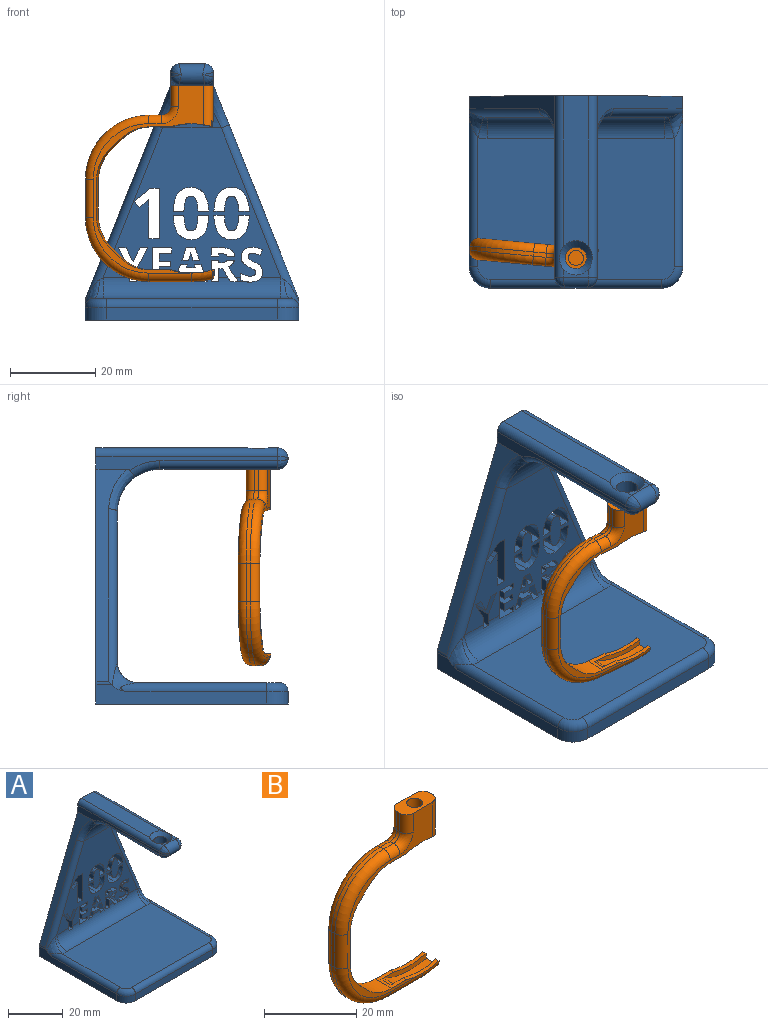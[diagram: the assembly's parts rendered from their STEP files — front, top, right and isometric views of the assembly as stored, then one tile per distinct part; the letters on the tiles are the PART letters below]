
ASSEMBLY  parts=2 mates=1
PART A: 194 faces, bbox 53.3x46.3x60.9 mm
  f0: plane 41.69x35.07mm, normal (0,-1,0), area 708mm2, adj f10,f11,f12,f15,f16,f17,f18,f19
  f1: plane 3.43x0.89mm, normal (0,-1,0), area 2.8mm2, adj f89,f90,f91,f191
  f2: plane 35.35x6mm, normal (0,0,1), area 206.5mm2, adj f9,f179,f180,f188
  f3: plane 2.17x2.04mm, normal (0,-1,0), area 3.1mm2, adj f97,f98,f99,f191
  f4: plane 40.93x5.54mm, normal (-1,0,0), area 127.7mm2, adj f5,f9,f162,f164,f169,f171,f193
  f5: plane 50x45mm, normal (0,0,-1), area 2239.3mm2, adj f4,f6,f8,f9,f161,f162
  f6: plane 40.93x5.54mm, normal (1,0,0), area 127.7mm2, adj f5,f9,f161,f167,f175,f177,f189
  f7: plane 46x33.29mm, normal (0,0,1), area 1514.6mm2, adj f164,f165,f166,f167,f168,f190,f191,f192
  f8: plane 40x3mm, normal (0,-1,0), area 120mm2, adj f5,f161,f162,f166
  f9: plane 60x50mm, normal (0,1,0), area 1525.4mm2, adj f2,f4,f5,f6,f10,f11,f12,f13
  f10: extruded ~5x1.53mm, area 9.4mm2, adj f0,f9,f11,f158
  f11: extruded ~5x1.31mm, area 7mm2, adj f0,f9,f10,f12
  f12: extruded ~5.02x1.69mm, area 9.7mm2, adj f0,f9,f11,f13,f191
  f13: extruded ~5.12x2.15mm, area 11.6mm2, adj f9,f12,f14,f191
  f14: extruded ~5.12x2.25mm, area 11.8mm2, adj f9,f13,f15,f191
  f15: plane 5.04x1.56mm, normal (1,0,0), area 7.8mm2, adj f0,f9,f14,f16,f191
  f16: extruded ~5x1.36mm, area 7.3mm2, adj f0,f9,f15,f17
  f17: extruded ~5x1.02mm, area 5.2mm2, adj f0,f9,f16,f18
  f18: extruded ~5x0.85mm, area 4.4mm2, adj f0,f9,f17,f19
  f19: extruded ~5x0.63mm, area 3.6mm2, adj f0,f9,f18,f20
  f20: extruded ~5x0.42mm, area 2.2mm2, adj f0,f9,f19,f21
  f21: extruded ~5x0.38mm, area 2.6mm2, adj f0,f9,f20,f22
  f22: extruded ~5x1.03mm, area 5.8mm2, adj f0,f9,f21,f23
  f23: extruded ~5x1.09mm, area 6.4mm2, adj f0,f9,f22,f24
  f24: extruded ~5x0.73mm, area 4.7mm2, adj f0,f9,f23,f25
  f25: extruded ~5x0.98mm, area 5mm2, adj f0,f9,f24,f26
  f26: extruded ~5x1.66mm, area 9.3mm2, adj f0,f9,f25,f27
  f27: extruded ~5x1.97mm, area 10.5mm2, adj f0,f9,f26,f28
  f28: extruded ~5x1.18mm, area 6mm2, adj f0,f9,f27,f29
  f29: extruded ~5x1.17mm, area 6.2mm2, adj f0,f9,f28,f30
  f30: plane 5x1.31mm, normal (-0.92,0,0.38), area 7.1mm2, adj f0,f9,f29,f31
  f31: extruded ~5x1.05mm, area 5.6mm2, adj f0,f9,f30,f32
  f32: extruded ~5x0.82mm, area 4.1mm2, adj f0,f9,f31,f33
  f33: extruded ~5x0.73mm, area 3.9mm2, adj f0,f9,f32,f34
  f34: extruded ~5x0.58mm, area 3.3mm2, adj f0,f9,f33,f35
  f35: extruded ~5x0.39mm, area 2mm2, adj f0,f9,f34,f36
  f36: extruded ~5x0.33mm, area 2.3mm2, adj f0,f9,f35,f158
  f37: plane 5x2.89mm, normal (0,0,-1), area 14.4mm2, adj f0,f9,f38,f146
  f38: plane 5.1x1.39mm, normal (-1,0,0), area 7mm2, adj f0,f9,f37,f39,f191
  f39: plane 5.1x4.57mm, normal (0,0,1), area 23.3mm2, adj f9,f38,f40,f191
  f40: plane 7.93x5.1mm, normal (1,0,0), area 39.7mm2, adj f0,f9,f39,f41,f191
  f41: plane 5x4.57mm, normal (0,0,-1), area 22.8mm2, adj f0,f9,f40,f42
  f42: plane 5x1.38mm, normal (-1,0,0), area 6.9mm2, adj f0,f9,f41,f43
  f43: plane 5x2.89mm, normal (0,0,1), area 14.4mm2, adj f0,f9,f42,f44
  f44: plane 5x1.74mm, normal (-1,0,0), area 8.7mm2, adj f0,f9,f43,f45
  f45: plane 5x2.69mm, normal (0,0,-1), area 13.4mm2, adj f0,f9,f44,f46
  f46: plane 5x1.38mm, normal (-1,0,0), area 6.9mm2, adj f0,f9,f45,f47
  f47: plane 5x2.69mm, normal (0,0,1), area 13.4mm2, adj f0,f9,f46,f146
  f48: plane 5x1.82mm, normal (0,0,-1), area 9.1mm2, adj f0,f9,f49,f147
  f49: plane 5x3.27mm, normal (-0.89,0,-0.45), area 18.3mm2, adj f0,f9,f48,f50
  f50: plane 5x3.27mm, normal (0.89,0,-0.45), area 18.3mm2, adj f0,f9,f49,f51
  f51: plane 5x1.81mm, normal (0,0,-1), area 9.1mm2, adj f0,f9,f50,f52
  f52: plane 5x4.85mm, normal (-0.88,0,0.48), area 27.6mm2, adj f0,f9,f51,f53
  f53: plane 5.1x3.09mm, normal (-1,0,0), area 15.5mm2, adj f0,f9,f52,f54,f191
  f54: plane 5.1x1.67mm, normal (0,0,1), area 8.5mm2, adj f9,f53,f55,f191
  f55: plane 5.1x3.03mm, normal (1,0,0), area 15.2mm2, adj f0,f9,f54,f147,f191
  f56: plane 5x2.5mm, normal (0,0,1), area 12.5mm2, adj f0,f9,f57,f148
  f57: extruded ~5x4.09mm, area 21.3mm2, adj f0,f9,f56,f58
  f58: extruded ~5x3.13mm, area 18.1mm2, adj f0,f9,f57,f59
  f59: extruded ~5x3.11mm, area 18.2mm2, adj f0,f9,f58,f60
  f60: extruded ~5x4.02mm, area 21mm2, adj f0,f9,f59,f61
  f61: plane 5x2.5mm, normal (0,0,1), area 12.5mm2, adj f0,f9,f60,f62
  f62: extruded ~5x2.59mm, area 13.2mm2, adj f0,f9,f61,f63
  f63: extruded ~5x1.27mm, area 8.5mm2, adj f0,f9,f62,f64
  f64: extruded ~5x1.27mm, area 8.5mm2, adj f0,f9,f63,f148
  f65: plane 5x2.07mm, normal (0,0,-1), area 10.3mm2, adj f0,f9,f66,f149
  f66: plane 11.9x5mm, normal (-1,0,0), area 59.5mm2, adj f0,f9,f65,f67
  f67: plane 5x2.52mm, normal (0,0,1), area 12.6mm2, adj f0,f9,f66,f68
  f68: plane 6.89x5mm, normal (1,0,0), area 34.4mm2, adj f0,f9,f67,f69
  f69: plane 5x1.13mm, normal (1,0,-0.02), area 5.7mm2, adj f0,f9,f68,f70
  f70: plane 5x1.24mm, normal (1,0,-0.03), area 6.2mm2, adj f0,f9,f69,f71
  f71: extruded ~5x0.87mm, area 6mm2, adj f0,f9,f70,f72
  f72: plane 5x1.37mm, normal (-0.63,0,0.78), area 8.8mm2, adj f0,f9,f71,f73
  f73: plane 5x1.51mm, normal (0.78,0,0.63), area 9.7mm2, adj f0,f9,f72,f149
  f74: plane 5x1.57mm, normal (0,0,1), area 7.9mm2, adj f0,f9,f75,f150
  f75: plane 5x2.97mm, normal (0.94,0,-0.33), area 15.7mm2, adj f0,f9,f74,f76
  f76: plane 5x2.06mm, normal (0,0,-1), area 10.3mm2, adj f0,f9,f75,f77
  f77: plane 5x2.97mm, normal (-0.94,0,-0.33), area 15.7mm2, adj f0,f9,f76,f78
  f78: plane 5x1.55mm, normal (0,0,1), area 7.8mm2, adj f0,f9,f77,f79
  f79: extruded ~5x1.2mm, area 6.3mm2, adj f0,f9,f78,f80
  f80: extruded ~5x0.53mm, area 2.8mm2, adj f0,f9,f79,f150
  f81: plane 5.1x4mm, normal (0.94,0,-0.33), area 21.2mm2, adj f0,f9,f82,f151,f191
  f82: plane 5x1.62mm, normal (0,0,-1), area 8.1mm2, adj f0,f9,f81,f83
  f83: extruded ~5x0.7mm, area 3.7mm2, adj f0,f9,f82,f84
  f84: plane 5x2.07mm, normal (0,0,-1), area 10.3mm2, adj f0,f9,f83,f85
  f85: extruded ~5x0.7mm, area 3.7mm2, adj f0,f9,f84,f86
  f86: plane 5x1.6mm, normal (0,0,-1), area 8mm2, adj f0,f9,f85,f87
  f87: plane 5.1x4mm, normal (-0.94,0,-0.33), area 21.2mm2, adj f0,f9,f86,f88,f191
  f88: plane 5.1x1.81mm, normal (0,0,1), area 9.2mm2, adj f9,f87,f89,f191
  f89: plane 5.1x1.89mm, normal (0.96,0,0.29), area 9.9mm2, adj f1,f9,f88,f90,f191
  f90: plane 5x2.89mm, normal (0,0,1), area 14.5mm2, adj f1,f9,f89,f91
  f91: plane 5.1x1.89mm, normal (-0.96,0,0.29), area 9.9mm2, adj f1,f9,f90,f151,f191
  f92: plane 5x1.74mm, normal (0,0,-1), area 8.7mm2, adj f0,f9,f93,f152
  f93: extruded ~5x0.69mm, area 3.8mm2, adj f0,f9,f92,f94
  f94: extruded ~5x1.09mm, area 7mm2, adj f0,f9,f93,f95
  f95: extruded ~5.1x3.46mm, area 20.9mm2, adj f0,f9,f94,f96,f191
  f96: plane 5.1x1.87mm, normal (0,0,1), area 9.5mm2, adj f9,f95,f97,f191
  f97: plane 5.1x3.05mm, normal (0.85,0,0.53), area 18mm2, adj f3,f9,f96,f98,f191
  f98: plane 5x0.89mm, normal (0,0,1), area 4.5mm2, adj f3,f9,f97,f99
  f99: plane 5.1x3.04mm, normal (-1,0,0), area 15.3mm2, adj f3,f9,f98,f100,f191
  f100: plane 5.1x1.68mm, normal (0,0,1), area 8.6mm2, adj f9,f99,f101,f191
  f101: plane 5.1x5mm, normal (1,0,0), area 25mm2, adj f0,f9,f100,f102,f191
  f102: plane 5x1.68mm, normal (0,0,-1), area 8.4mm2, adj f0,f9,f101,f103
  f103: plane 5x0.59mm, normal (-1,0,0), area 2.9mm2, adj f0,f9,f102,f104
  f104: plane 5x0.54mm, normal (0,0,-1), area 2.7mm2, adj f0,f9,f103,f105
  f105: extruded ~5x1.18mm, area 6.1mm2, adj f0,f9,f104,f152
  f106: extruded ~5x1.34mm, area 7.9mm2, adj f0,f9,f107,f153
  f107: plane 5x1.77mm, normal (0,0,1), area 8.8mm2, adj f0,f9,f106,f108
  f108: extruded ~5x0.32mm, area 2.2mm2, adj f0,f9,f107,f109
  f109: extruded ~5x1.2mm, area 6.2mm2, adj f0,f9,f108,f110
  f110: plane 5x0.51mm, normal (0,0,1), area 2.6mm2, adj f0,f9,f109,f111
  f111: plane 5x0.55mm, normal (-1,0,0), area 2.8mm2, adj f0,f9,f110,f112
  f112: plane 5x1.68mm, normal (0,0,1), area 8.4mm2, adj f0,f9,f111,f113
  f113: plane 5x1.93mm, normal (1,0,0), area 9.7mm2, adj f0,f9,f112,f114
  f114: plane 5x2.31mm, normal (0,0,-1), area 11.6mm2, adj f0,f9,f113,f153
  f115: plane 5x2.5mm, normal (0,0,-1), area 12.5mm2, adj f0,f9,f116,f154
  f116: extruded ~5x4.17mm, area 21.7mm2, adj f0,f9,f115,f117
  f117: extruded ~5x3.15mm, area 18.2mm2, adj f0,f9,f116,f118
  f118: extruded ~5x3.11mm, area 18.1mm2, adj f0,f9,f117,f119
  f119: extruded ~5x4.12mm, area 21.5mm2, adj f0,f9,f118,f120
  f120: plane 5x2.5mm, normal (0,0,-1), area 12.5mm2, adj f0,f9,f119,f121
  f121: extruded ~5x2.69mm, area 13.6mm2, adj f0,f9,f120,f122
  f122: extruded ~5x1.27mm, area 8.5mm2, adj f0,f9,f121,f123
  f123: extruded ~5x1.27mm, area 8.5mm2, adj f0,f9,f122,f154
  f124: plane 5x2.5mm, normal (0,0,-1), area 12.5mm2, adj f0,f9,f125,f155
  f125: extruded ~5x4.17mm, area 21.7mm2, adj f0,f9,f124,f126
  f126: extruded ~5x3.15mm, area 18.2mm2, adj f0,f9,f125,f127
  f127: extruded ~5x3.11mm, area 18.1mm2, adj f0,f9,f126,f128
  f128: extruded ~5x4.12mm, area 21.5mm2, adj f0,f9,f127,f129
  f129: plane 5x2.5mm, normal (0,0,-1), area 12.5mm2, adj f0,f9,f128,f130
  f130: extruded ~5x2.69mm, area 13.6mm2, adj f0,f9,f129,f131
  f131: extruded ~5x1.27mm, area 8.5mm2, adj f0,f9,f130,f132
  f132: extruded ~5x1.27mm, area 8.5mm2, adj f0,f9,f131,f155
  f133: extruded ~5x4.02mm, area 21mm2, adj f0,f9,f134,f156
  f134: plane 5x2.5mm, normal (0,0,1), area 12.5mm2, adj f0,f9,f133,f135
  f135: extruded ~5x2.59mm, area 13.2mm2, adj f0,f9,f134,f136
  f136: extruded ~5x1.27mm, area 8.5mm2, adj f0,f9,f135,f137
  f137: extruded ~5x1.27mm, area 8.5mm2, adj f0,f9,f136,f138
  f138: extruded ~5x2.59mm, area 13.2mm2, adj f0,f9,f137,f139
  f139: plane 5x2.5mm, normal (0,0,1), area 12.5mm2, adj f0,f9,f138,f140
  f140: extruded ~5x4.09mm, area 21.3mm2, adj f0,f9,f139,f141
  f141: extruded ~5x3.13mm, area 18.1mm2, adj f0,f9,f140,f156
  f142: plane 42.5x3.24mm, normal (-1,0,0), area 63.6mm2, adj f9,f143,f170,f172,f173,f180,f183
  f143: plane 49.64x19.86mm, normal (-0.93,0,0.37), area 173.7mm2, adj f9,f142,f169,f171,f173
  f144: plane 49.64x19.86mm, normal (0.93,0,0.37), area 173.7mm2, adj f9,f145,f175,f177,f178
  f145: plane 42.5x3.24mm, normal (1,0,0), area 63.6mm2, adj f9,f144,f174,f176,f178,f179,f184
  f146: plane 5x2.05mm, normal (-1,0,0), area 10.2mm2, adj f0,f9,f37,f47
  f147: plane 5x4.9mm, normal (0.88,0,0.47), area 27.8mm2, adj f0,f9,f48,f55
  f148: extruded ~5x2.59mm, area 13.2mm2, adj f0,f9,f56,f64
  f149: plane 5x3.83mm, normal (0.62,0,-0.78), area 24.5mm2, adj f0,f9,f65,f73
  f150: extruded ~5x1.73mm, area 9mm2, adj f0,f9,f74,f80
  f151: plane 5.1x1.81mm, normal (0,0,1), area 9.2mm2, adj f9,f81,f91,f191
  f152: extruded ~5x0.32mm, area 2.1mm2, adj f0,f9,f92,f105
  f153: extruded ~5x2.39mm, area 12.5mm2, adj f0,f9,f106,f114
  f154: extruded ~5x2.68mm, area 13.6mm2, adj f0,f9,f115,f123
  f155: extruded ~5x2.68mm, area 13.6mm2, adj f0,f9,f124,f132
  f156: extruded ~5x3.11mm, area 18.2mm2, adj f0,f9,f133,f141
  f157: plane 6x1.85mm, normal (0,0,1), area 5.5mm2, adj f179,f180,f185,f188
  f158: extruded ~5x1.07mm, area 6mm2, adj f0,f9,f10,f36
  f159: plane 27.5x6mm, normal (0,0,-1), area 145.4mm2, adj f160,f163,f170,f174,f185
  f160: cylinder r=2.5mm len=5mm, axis (0,0,1), area 55mm2, adj f159,f188
  f161: cylinder r=5mm len=5mm, axis (0,0,-1), area 23.6mm2, adj f5,f6,f8,f168
  f162: cylinder r=5mm len=5mm, axis (0,0,1), area 23.6mm2, adj f4,f5,f8,f165
  f163: cylinder r=10mm len=13.69mm, axis (-1,0,0), area 130mm2, adj f0,f159,f172,f173,f176,f178
  f164: cylinder r=2mm len=34.17mm, axis (0,-1,0), area 102.7mm2, adj f4,f7,f165,f193
  f165: torus R=3mm, axis (0,0,1), area 21.1mm2, adj f7,f162,f164,f166
  f166: cylinder r=2mm len=40mm, axis (1,0,0), area 125.7mm2, adj f7,f8,f165,f168
  f167: cylinder r=2mm len=34.17mm, axis (0,1,0), area 102.7mm2, adj f6,f7,f168,f189
  f168: torus R=3mm, axis (0,0,1), area 21.1mm2, adj f7,f161,f166,f167
  f169: cylinder r=2mm len=3.74mm, axis (0,1,0), area 2.6mm2, adj f4,f9,f143,f171
  f170: cylinder r=2mm len=27.5mm, axis (0,1,0), area 86.4mm2, adj f142,f159,f172,f182
  f171: cylinder r=2mm len=41.9mm, axis (0.37,0,0.93), area 128.9mm2, adj f0,f4,f143,f169,f173,f192,f193
  f172: torus R=12mm, axis (1,0,0), area 21.1mm2, adj f142,f163,f170,f173
  f173: bspline ~10.36x6.07mm, area 36mm2, adj f142,f143,f163,f171,f172
  f174: cylinder r=2mm len=27.5mm, axis (0,-1,0), area 86.4mm2, adj f145,f159,f176,f181
  f175: cylinder r=2mm len=3.74mm, axis (0,1,0), area 2.6mm2, adj f6,f9,f144,f177
  f176: torus R=12mm, axis (1,0,0), area 21.1mm2, adj f145,f163,f174,f178
  f177: cylinder r=2mm len=41.9mm, axis (0.37,0,-0.93), area 128.9mm2, adj f0,f6,f144,f175,f178,f189,f190
  f178: bspline ~10.36x6.07mm, area 36mm2, adj f144,f145,f163,f176,f177
  f179: cylinder r=2mm len=42.5mm, axis (0,1,0), area 131.3mm2, adj f2,f9,f145,f157,f187,f188
  f180: cylinder r=2mm len=42.5mm, axis (0,-1,0), area 130.4mm2, adj f2,f9,f142,f157,f186,f188
  f181: bspline ~2.65x2.5mm, area 5.5mm2, adj f174,f184,f185
  f182: bspline ~2.65x2.5mm, area 5.5mm2, adj f170,f183,f185
  f183: cylinder r=2.5mm len=2.5mm, axis (0,0,1), area 2mm2, adj f142,f182,f186
  f184: cylinder r=2.5mm len=2.5mm, axis (0,0,-1), area 2mm2, adj f145,f181,f187
  f185: cylinder r=2.5mm len=6mm, axis (-1,0,0), area 43.2mm2, adj f157,f159,f181,f182,f186,f187
  f186: bspline ~2.65x2.5mm, area 5.5mm2, adj f180,f183,f185
  f187: bspline ~2.65x2.5mm, area 5.5mm2, adj f179,f184,f185
  f188: cone r=2.5mm half-angle=45deg, axis (0,0,1), area 42.6mm2, adj f2,f157,f160,f179,f180
  f189: bspline ~8.52x5.97mm, area 20.2mm2, adj f6,f167,f177,f190
  f190: bspline ~5.08x5mm, area 10.2mm2, adj f7,f177,f189,f191
  f191: cylinder r=5mm len=41.69mm, axis (-1,0,0), area 310.2mm2, adj f0,f1,f3,f7,f12,f13,f14,f15
  f192: bspline ~5.08x5mm, area 10.2mm2, adj f7,f171,f191,f193
  f193: bspline ~8.52x5.97mm, area 20.2mm2, adj f4,f164,f171,f192
PART B: 54 faces, bbox 31.9x5x47.2 mm
  f0: plane 44x26mm, normal (0,-1,0), area 118.9mm2, adj f2,f7,f8,f9,f10,f11,f17,f18
  f1: plane 44x26mm, normal (0,1,0), area 118.9mm2, adj f2,f3,f6,f7,f8,f9,f11,f18
  f2: plane 5x4.64mm, normal (0,0,-1), area 11.7mm2, adj f0,f1,f3,f10,f23,f24,f42,f44
  f3: cylinder r=17.5mm len=9.73mm, axis (0,1,0), area 9.3mm2, adj f1,f2,f23,f40
  f4: plane 8.43x1mm, normal (1,0,0), area 8.4mm2, adj f11,f22,f40,f41
  f5: plane 5x2.08mm, normal (1,0,0), area 4.7mm2, adj f6,f16,f17,f19,f20,f21,f27,f33
  f6: cylinder r=17.5mm len=10mm, axis (0,1,0), area 10.1mm2, adj f1,f5,f7,f20,f27
  f7: plane 5x4.64mm, normal (0,0,1), area 11.7mm2, adj f0,f1,f6,f17,f19,f20,f43,f45
  f8: plane 8.29x5mm, normal (1,0,0), area 41.4mm2, adj f0,f1,f46,f47
  f9: plane 5x2.63mm, normal (0.71,0,-0.71), area 18.6mm2, adj f0,f1,f44,f47
  f10: cylinder r=17.5mm len=9.73mm, axis (0,1,0), area 9.3mm2, adj f0,f2,f24,f41
  f11: plane 10x5mm, normal (0,0,1), area 36.9mm2, adj f0,f1,f4,f12,f25,f31,f35,f40
  f12: plane 5x1mm, normal (-1,0,0), area 5mm2, adj f11,f31,f34,f35
  f13: plane 3x1mm, normal (0,0,1), area 3mm2, adj f30,f34,f39,f49
  f14: plane 9x1mm, normal (-1,0,0), area 9mm2, adj f29,f38,f49,f52
  f15: plane 10x1mm, normal (0,0,-1), area 10mm2, adj f16,f28,f36,f52
  f16: cylinder r=19.5mm len=5mm, axis (0,1,0), area 5.1mm2, adj f5,f15,f27,f33
  f17: cylinder r=17.5mm len=10mm, axis (0,1,0), area 10.1mm2, adj f0,f5,f7,f19,f33
  f18: plane 5x2.63mm, normal (0.71,0,0.71), area 18.6mm2, adj f0,f1,f45,f46
  f19: plane 13.84x1.98mm, normal (0,1,0), area 15.1mm2, adj f5,f7,f17,f21,f43
  f20: plane 13.84x1.98mm, normal (0,-1,0), area 15.1mm2, adj f5,f6,f7,f21,f43
  f21: cylinder r=18.75mm len=12.99mm, axis (0,-1,0), area 40mm2, adj f5,f19,f20,f43
  f22: cylinder r=18.75mm len=12.99mm, axis (0,-1,0), area 39.8mm2, adj f4,f23,f24,f40,f41,f42
  f23: plane 13.58x1.98mm, normal (0,-1,0), area 14.7mm2, adj f2,f3,f22,f40,f42
  f24: plane 13.58x1.98mm, normal (0,1,0), area 14.7mm2, adj f2,f10,f22,f41,f42
  f25: cylinder r=1.75mm len=6mm, axis (0,0,1), area 66mm2, adj f11,f26
  f26: plane 3.5x3.5mm, normal (0,0,1), area 9.6mm2, adj f25
  f27: torus R=17.5mm, axis (0,-1,0), area 15.9mm2, adj f5,f6,f16,f28
  f28: cylinder r=2mm len=10mm, axis (1,0,0), area 31.4mm2, adj f1,f15,f27,f53
  f29: cylinder r=2mm len=9mm, axis (0,0,-1), area 28.3mm2, adj f1,f14,f50,f53
  f30: cylinder r=2mm len=3mm, axis (-1,0,0), area 9.4mm2, adj f1,f13,f32,f50
  f31: cylinder r=2mm len=5mm, axis (0,0,-1), area 15.7mm2, adj f1,f11,f12,f32
  f32: torus R=4mm, axis (0,-1,0), area 13.5mm2, adj f1,f30,f31,f34
  f33: torus R=17.5mm, axis (0,-1,0), area 15.9mm2, adj f5,f16,f17,f36
  f34: cylinder r=2mm len=2mm, axis (0,-1,0), area 3.1mm2, adj f12,f13,f32,f37
  f35: cylinder r=2mm len=5mm, axis (0,0,1), area 15.7mm2, adj f0,f11,f12,f37
  f36: cylinder r=2mm len=10mm, axis (-1,0,0), area 31.4mm2, adj f0,f15,f33,f51
  f37: torus R=4mm, axis (0,-1,0), area 13.5mm2, adj f0,f34,f35,f39
  f38: cylinder r=2mm len=9mm, axis (0,0,1), area 28.3mm2, adj f0,f14,f48,f51
  f39: cylinder r=2mm len=3mm, axis (1,0,0), area 9.4mm2, adj f0,f13,f37,f48
  f40: cylinder r=2mm len=9.65mm, axis (0,0,1), area 28.6mm2, adj f1,f3,f4,f11,f22,f23
  f41: cylinder r=2mm len=9.65mm, axis (0,0,-1), area 28.6mm2, adj f0,f4,f10,f11,f22,f24
  f42: cylinder r=2mm len=3mm, axis (0,-1,0), area 2.6mm2, adj f2,f22,f23,f24
  f43: cylinder r=2mm len=3mm, axis (0,-1,0), area 2.6mm2, adj f7,f19,f20,f21
  f44: cylinder r=10mm len=7.07mm, axis (0,1,0), area 39.3mm2, adj f0,f1,f2,f9
  f45: cylinder r=10mm len=7.07mm, axis (0,1,0), area 39.3mm2, adj f0,f1,f7,f18
  f46: cylinder r=10mm len=7.07mm, axis (0,-1,0), area 39.3mm2, adj f0,f1,f8,f18
  f47: cylinder r=10mm len=7.07mm, axis (0,1,0), area 39.3mm2, adj f0,f1,f8,f9
  f48: torus R=13mm, axis (0,-1,0), area 70.4mm2, adj f0,f38,f39,f49
  f49: cylinder r=15mm len=15mm, axis (0,1,0), area 23.6mm2, adj f13,f14,f48,f50
  f50: torus R=13mm, axis (0,-1,0), area 70.4mm2, adj f1,f29,f30,f49
  f51: torus R=13mm, axis (0,-1,0), area 70.4mm2, adj f0,f36,f38,f52
  f52: cylinder r=15mm len=15mm, axis (0,1,0), area 23.6mm2, adj f14,f15,f51,f53
  f53: torus R=13mm, axis (0,-1,0), area 70.4mm2, adj f1,f28,f29,f52
PLACE A t=(-6.87,33.18,-1.55)mm fixed
PLACE B rot(axis=(0,0,-1),5.3deg) t=(-6.87,-4.82,26.95)mm
MATE revolute A.f160 <-> B.f25  axis (0,0,1) through (-6.87,-4.82,53.45)mm
